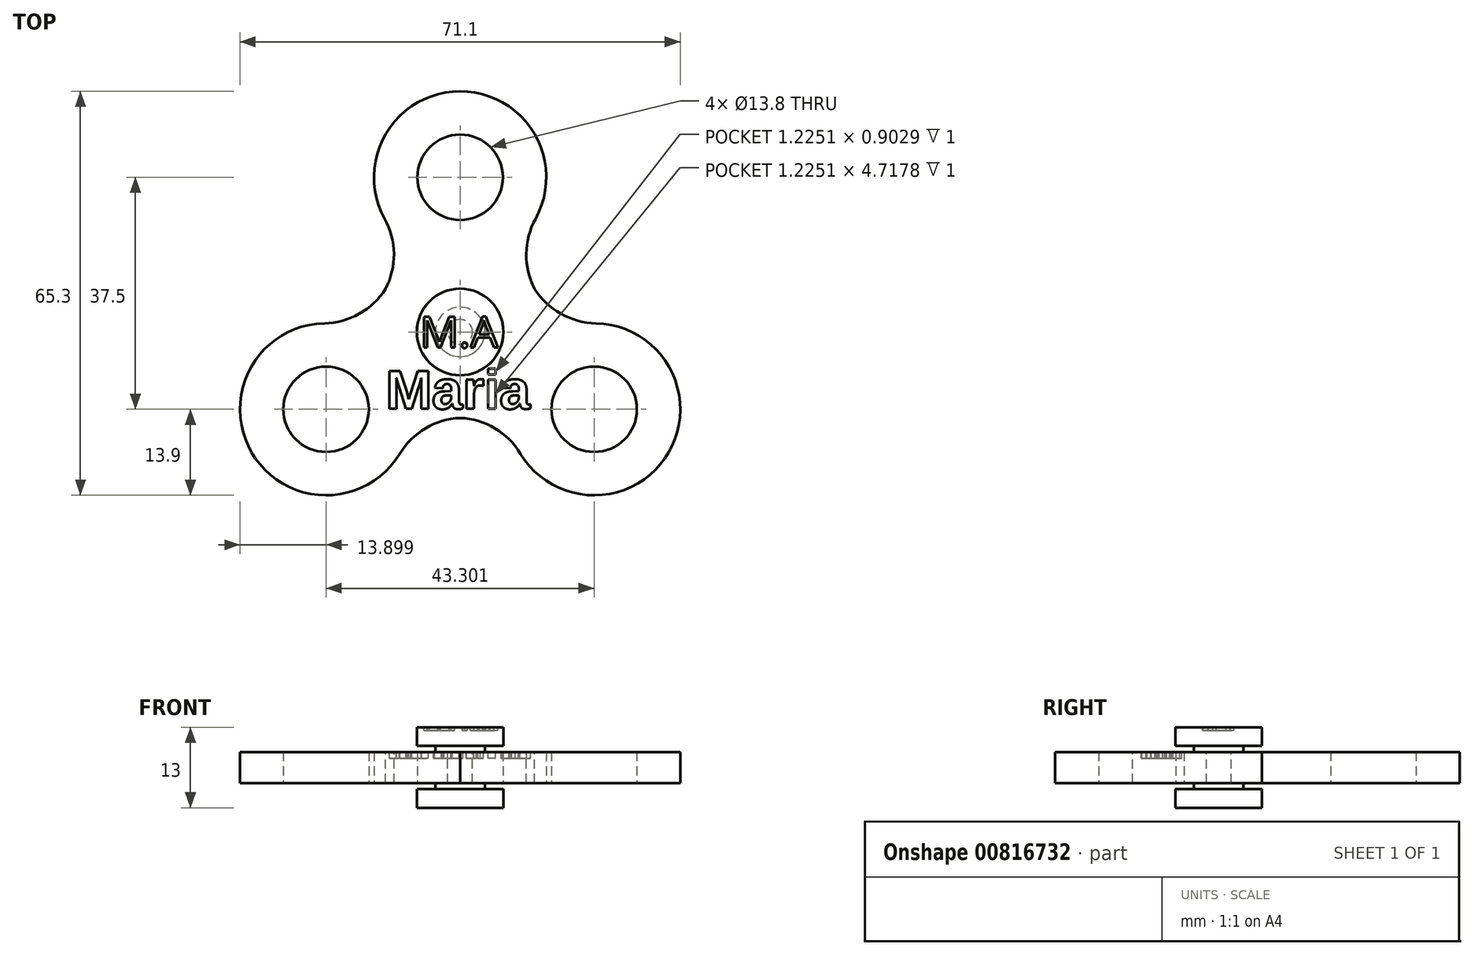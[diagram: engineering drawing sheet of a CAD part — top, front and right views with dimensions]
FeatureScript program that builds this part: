
annotation { "Feature Type Name" : "Feature", "Feature Type Description" : "" }
export const myFeature = defineFeature(function(context is Context, id is Id, definition is map)
    precondition{}
    {
        {
            var Q0;
            Q0=qCreatedBy(makeId("Top.planeOp"),FACE);
            var sketch = newSketch(context, id + "F0", { "sketchPlane" : qUnion([Q0])});
            skCircle(sketch, "E0", {"center": v(0, 0) * mm, "radius": 6.9 * mm});
            skCircle(sketch, "E1", {"center": v(0, 0) * mm, "radius": 25 * mm, "construction": true});
            skCircle(sketch, "E2", {"center": v(0, 25) * mm, "radius": 6.9 * mm});
            skCircle(sketch, "E3.1.0", {"center": v(-21.65, -12.5) * mm, "radius": 6.9 * mm});
            skCircle(sketch, "E3.2.0", {"center": v(21.65, -12.5) * mm, "radius": 6.9 * mm});
            skLineSegment(sketch, "E4", {"start": v(0, 25) * mm, "end": v(0, 0) * mm, "construction": true});
            skLineSegment(sketch, "E5", {"start": v(21.65, -12.5) * mm, "end": v(0, 0) * mm, "construction": true});
            skArc(sketch, "E6.0", {"start": v(6.08, 12.5) * mm, "mid": v(0, 38.9) * mm, "end": v(-6.08, 12.5) * mm});
            skArc(sketch, "E7.0", {"start": v(7.79, -11.51) * mm, "mid": v(33.69, -19.45) * mm, "end": v(13.87, -0.99) * mm});
            skArc(sketch, "E8.0", {"start": v(-13.87, -0.99) * mm, "mid": v(-33.69, -19.45) * mm, "end": v(-7.79, -11.51) * mm});
            skArc(sketch, "E9.0", {"start": v(-6.08, 12.5) * mm, "mid": v(-12.04, 6.95) * mm, "end": v(-13.87, -0.99) * mm});
            skArc(sketch, "E10.trimOffspring", {"start": v(13.87, -0.99) * mm, "mid": v(12.04, 6.95) * mm, "end": v(6.08, 12.5) * mm});
            skArc(sketch, "E11.trimOffspring", {"start": v(-7.79, -11.51) * mm, "mid": v(0, -13.9) * mm, "end": v(7.79, -11.51) * mm});
            skSolve(sketch);
        }
        {
            var Q0;
            Q0 = qSketchRegion(id + "F0", true);
            extrude(context, id + "F1", {"entities" : qUnion([Q0]), "endBound" : BoundingType.SYMMETRIC, "depth" : 5 * mm, "offsetDistance" : 25 * mm});
        }
        {
            var Q0;
            Q0=makeQuery(id+"F1.opExtrude","SWEPT_EDGE",EDGE,{"disambiguationData":[OSD([sQuery(id+"F0.wireOp",EDGE,"E8.0"),sQuery(id+"F0.wireOp",EDGE,"E11.trimOffspring")])]});
            var Q1;
            Q1=makeQuery(id+"F1.opExtrude","SWEPT_EDGE",EDGE,{"disambiguationData":[OSD([sQuery(id+"F0.wireOp",EDGE,"E7.0"),sQuery(id+"F0.wireOp",EDGE,"E11.trimOffspring")])]});
            var Q2;
            Q2=makeQuery(id+"F1.opExtrude","SWEPT_EDGE",EDGE,{"disambiguationData":[OSD([sQuery(id+"F0.wireOp",EDGE,"E7.0"),sQuery(id+"F0.wireOp",EDGE,"E10.trimOffspring")])]});
            var Q3;
            Q3=makeQuery(id+"F1.opExtrude","SWEPT_EDGE",EDGE,{"disambiguationData":[OSD([sQuery(id+"F0.wireOp",EDGE,"E6.0"),sQuery(id+"F0.wireOp",EDGE,"E10.trimOffspring")])]});
            var Q4;
            Q4=makeQuery(id+"F1.opExtrude","SWEPT_EDGE",EDGE,{"disambiguationData":[OSD([sQuery(id+"F0.wireOp",EDGE,"E6.0"),sQuery(id+"F0.wireOp",EDGE,"E9.0")])]});
            var Q5;
            Q5=makeQuery(id+"F1.opExtrude","SWEPT_EDGE",EDGE,{"disambiguationData":[OSD([sQuery(id+"F0.wireOp",EDGE,"E8.0"),sQuery(id+"F0.wireOp",EDGE,"E9.0")])]});
            fillet(context, id + "F2", {"entities" : qUnion([Q0, Q1, Q2, Q3, Q4, Q5]), "radius" : 12 * mm, "tangentPropagation" : true, "allowEdgeOverflow" : false});
        }
        {
            var Q0;
            Q0=qCreatedBy(makeId("Front.planeOp"),FACE);
            var sketch = newSketch(context, id + "F3", { "sketchPlane" : qUnion([Q0])});
            skLineSegment(sketch, "E12.0", {"start": v(-6.9, 2.5) * mm, "end": v(6.9, 2.5) * mm, "construction": true});
            skLineSegment(sketch, "E13", {"start": v(0, 6.5) * mm, "end": v(0, -5.5) * mm});
            skLineSegment(sketch, "E14", {"start": v(0, 6.5) * mm, "end": v(7, 6.5) * mm});
            skLineSegment(sketch, "E15", {"start": v(7, 6.5) * mm, "end": v(7, 3.5) * mm});
            skLineSegment(sketch, "E16", {"start": v(7, 3.5) * mm, "end": v(4, 3.5) * mm});
            skLineSegment(sketch, "E17", {"start": v(4, 3.5) * mm, "end": v(4, 2.5) * mm});
            skLineSegment(sketch, "E18", {"start": v(4, 2.5) * mm, "end": v(2, 2.5) * mm});
            skLineSegment(sketch, "E19", {"start": v(2, 2.5) * mm, "end": v(2, -5.5) * mm});
            skLineSegment(sketch, "E20", {"start": v(2, -5.5) * mm, "end": v(0, -5.5) * mm});
            skSolve(sketch);
        }
        {
            var Q0;
            Q0 = qSketchRegion(id + "F3", true);
            var Q1;
            Q1=sQuery(id+"F3.wireOp",EDGE,"E13");
            revolve(context, id + "F4", {"surfaceOperationType" : NewSurfaceOperationType.NEW, "entities" : qUnion([Q0]), "axis" : qUnion([Q1]), "revolveType" : RevolveType.FULL});
        }
        {
            var Q0;
            Q0=makeQuery(id+"F4.opRevolve","SWEPT_FACE",FACE,{"disambiguationData":[OSD([sQuery(id+"F3.wireOp",EDGE,"E20")])]});
            var sketch = newSketch(context, id + "F5", { "sketchPlane" : qUnion([Q0])});
            skCircle(sketch, "E21", {"center": v(0, 0) * mm, "radius": 2.75 * mm});
            skCircle(sketch, "E22", {"center": v(0, 0) * mm, "radius": 7 * mm});
            skSolve(sketch);
        }
        {
            var Q0;
            Q0 = qSketchRegion(id + "F5", true);
            extrude(context, id + "F6", {"entities" : qUnion([Q0]), "oppositeDirection" : true, "depth" : 2 * mm, "offsetDistance" : 25 * mm});
        }
        {
            var Q0;
            Q0=makeQuery(id+"F6.opExtrude","CAP_FACE",FACE,{"disambiguationData":[OSD([sQuery(id+"F5.wireOp",EDGE,"E21"),sQuery(id+"F5.wireOp",EDGE,"E22")])],"isStart":true});
            var sketch = newSketch(context, id + "F7", { "sketchPlane" : qUnion([Q0])});
            skCircle(sketch, "E23.0", {"center": v(0, 0) * mm, "radius": 7 * mm});
            skSolve(sketch);
        }
        {
            var Q0;
            Q0 = qSketchRegion(id + "F7", true);
            extrude(context, id + "F8", {"entities" : qUnion([Q0]), "depth" : 1 * mm, "offsetDistance" : 25 * mm});
        }
        {
            var Q0;
            Q0=makeQuery(id+"F6.opExtrude","CAP_FACE",FACE,{"disambiguationData":[OSD([sQuery(id+"F5.wireOp",EDGE,"E21"),sQuery(id+"F5.wireOp",EDGE,"E22")])],"isStart":false});
            var sketch = newSketch(context, id + "F9", { "sketchPlane" : qUnion([Q0])});
            skCircle(sketch, "E24.0", {"center": v(0, 0) * mm, "radius": 4 * mm});
            skCircle(sketch, "E25.0", {"center": v(0, 0) * mm, "radius": 2 * mm});
            skSolve(sketch);
        }
        {
            var Q0;
            Q0 = qSketchRegion(id + "F9", true);
            extrude(context, id + "F10", {"entities" : qUnion([Q0]), "depth" : 1 * mm, "offsetDistance" : 25 * mm});
        }
        {
            var Q0;
            Q0=makeQuery(id+"F4.opRevolve","SWEPT_FACE",FACE,{"disambiguationData":[OSD([sQuery(id+"F3.wireOp",EDGE,"E14")])]});
            var sketch = newSketch(context, id + "F11", { "sketchPlane" : qUnion([Q0])});
            skText(sketch, "E26", { "text": "M.A", "fontName": "OpenSans-Regular.ttf"});
            const initialGuessF11  = {"E26": [-0.00653, -0.00252, 1, 0, 0.00504]};
            skSetInitialGuess(sketch, initialGuessF11);
            skSolve(sketch);
        }
        {
            var Q0;
            Q0 = qSketchRegion(id + "F11", true);
            extrude(context, id + "F12", {"entities" : qUnion([Q0]), "operationType" : NewBodyOperationType.REMOVE, "oppositeDirection" : true, "depth" : 0.5 * mm, "offsetDistance" : 25 * mm});
        }
        {
            var Q0;
            Q0=makeQuery(id+"F1.opExtrude","CAP_FACE",FACE,{"disambiguationData":[OSD([sQuery(id+"F0.wireOp",EDGE,"E0"),sQuery(id+"F0.wireOp",EDGE,"E2"),sQuery(id+"F0.wireOp",EDGE,"E3.1.0"),sQuery(id+"F0.wireOp",EDGE,"E3.2.0"),sQuery(id+"F0.wireOp",EDGE,"E6.0"),sQuery(id+"F0.wireOp",EDGE,"E7.0"),sQuery(id+"F0.wireOp",EDGE,"E8.0"),sQuery(id+"F0.wireOp",EDGE,"E9.0"),sQuery(id+"F0.wireOp",EDGE,"E10.trimOffspring"),sQuery(id+"F0.wireOp",EDGE,"E11.trimOffspring")])],"isStart":false});
            var sketch = newSketch(context, id + "F13", { "sketchPlane" : qUnion([Q0])});
            skText(sketch, "E27", { "text": "Maria", "fontName": "Arimo-Bold.ttf"});
            const initialGuessF13  = {"E27": [-0.012, -0.01243, 1, 0, 0.00643]};
            skSetInitialGuess(sketch, initialGuessF13);
            skSolve(sketch);
        }
        {
            var Q0;
            Q0 = qSketchRegion(id + "F13", true);
            extrude(context, id + "F14", {"entities" : qUnion([Q0]), "operationType" : NewBodyOperationType.REMOVE, "oppositeDirection" : true, "depth" : 1 * mm, "offsetDistance" : 25 * mm});
        }
        {
            var Q0;
            Q0=makeQuery(id+"F10.opExtrude","CAP_FACE",FACE,{"disambiguationData":[OSD([sQuery(id+"F9.wireOp",EDGE,"E24.0"),sQuery(id+"F9.wireOp",EDGE,"E25.0")])],"isStart":false});
            var sketch = newSketch(context, id + "F15", { "sketchPlane" : qUnion([Q0])});
            skCircle(sketch, "E28.0", {"center": v(0, 0) * mm, "radius": 2 * mm});
            skCircle(sketch, "E29.0", {"center": v(0, 0) * mm, "radius": 4 * mm});
            skSolve(sketch);
        }
        {
            var Q0;
            Q0 = qSketchRegion(id + "F15", true);
            var Q1;
            Q1=makeQuery(id+"F8.opExtrude","CAP_FACE",FACE,{"disambiguationData":[OSD([sQuery(id+"F7.wireOp",EDGE,"E23.0")])],"isStart":false});
            extrude(context, id + "F16", {"entities" : qUnion([Q0]), "operationType" : NewBodyOperationType.ADD, "endBound" : BoundingType.UP_TO_SURFACE, "oppositeDirection" : true, "depth" : 25 * mm, "endBoundEntityFace" : qUnion([Q1]), "offsetDistance" : 25 * mm});
        }
    });
